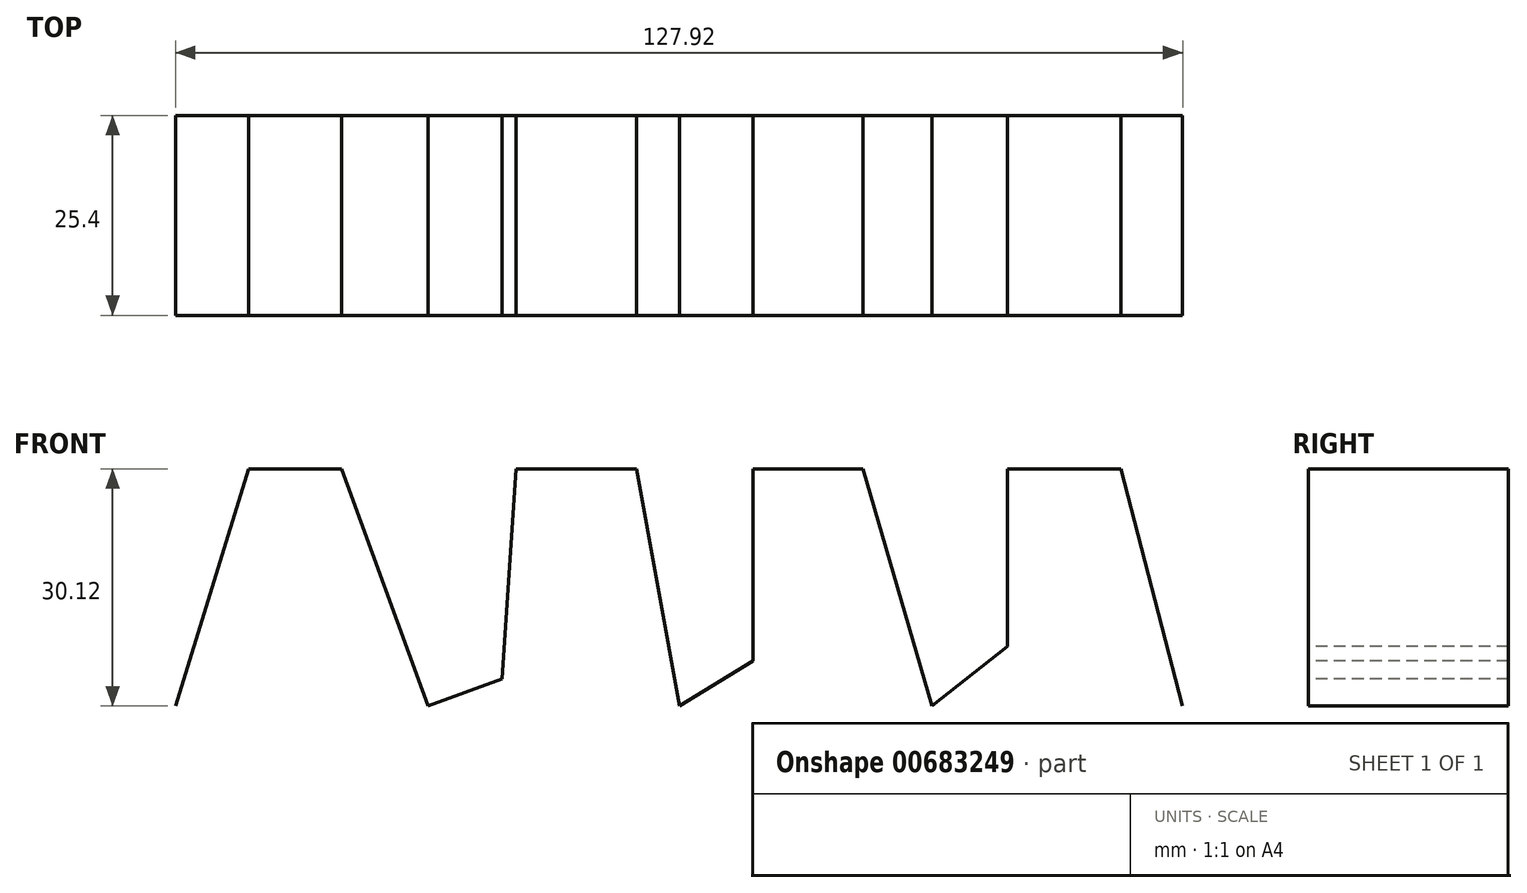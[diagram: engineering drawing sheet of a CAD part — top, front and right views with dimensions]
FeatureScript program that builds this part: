
annotation { "Feature Type Name" : "Feature", "Feature Type Description" : "" }
export const myFeature = defineFeature(function(context is Context, id is Id, definition is map)
    precondition{}
    {
        {
            var Q0;
            Q0=qCreatedBy(makeId("Front.planeOp"),FACE);
            var sketch = newSketch(context, id + "F0", { "sketchPlane" : qUnion([Q0])});
            skLineSegment(sketch, "E0", {"start": v(-63.99, 0) * mm, "end": v(-54.75, 30.12) * mm});
            skLineSegment(sketch, "E1", {"start": v(-54.75, 30.12) * mm, "end": v(-42.93, 30.12) * mm});
            skLineSegment(sketch, "E2", {"start": v(-42.93, 30.12) * mm, "end": v(-31.94, 0) * mm});
            skLineSegment(sketch, "E3", {"start": v(-31.94, 0) * mm, "end": v(-22.51, 3.44) * mm});
            skLineSegment(sketch, "E4", {"start": v(-22.51, 3.44) * mm, "end": v(-20.77, 30.12) * mm});
            skLineSegment(sketch, "E5", {"start": v(-20.77, 30.12) * mm, "end": v(-5.47, 30.12) * mm});
            skLineSegment(sketch, "E6", {"start": v(-5.47, 30.12) * mm, "end": v(0, 0) * mm});
            skLineSegment(sketch, "E7", {"start": v(0, 0) * mm, "end": v(9.35, 5.71) * mm});
            skLineSegment(sketch, "E8", {"start": v(9.35, 5.71) * mm, "end": v(9.35, 30.12) * mm});
            skLineSegment(sketch, "E9", {"start": v(9.35, 30.12) * mm, "end": v(23.32, 30.12) * mm});
            skLineSegment(sketch, "E10", {"start": v(23.32, 30.12) * mm, "end": v(32.05, 0) * mm});
            skLineSegment(sketch, "E11", {"start": v(32.05, 0) * mm, "end": v(41.66, 7.57) * mm});
            skLineSegment(sketch, "E12", {"start": v(41.66, 7.57) * mm, "end": v(41.66, 30.12) * mm});
            skLineSegment(sketch, "E13", {"start": v(41.66, 30.12) * mm, "end": v(56.07, 30.12) * mm});
            skLineSegment(sketch, "E14", {"start": v(56.07, 30.12) * mm, "end": v(63.93, 0) * mm});
            skSolve(sketch);
        }
        {
            var Q0;
            Q0=sQuery(id+"F0.wireOp",EDGE,"E14");
            var Q1;
            Q1=sQuery(id+"F0.wireOp",EDGE,"E13");
            var Q2;
            Q2=sQuery(id+"F0.wireOp",EDGE,"E12");
            var Q3;
            Q3=sQuery(id+"F0.wireOp",EDGE,"E11");
            var Q4;
            Q4=sQuery(id+"F0.wireOp",EDGE,"E10");
            var Q5;
            Q5=sQuery(id+"F0.wireOp",EDGE,"E9");
            var Q6;
            Q6=sQuery(id+"F0.wireOp",EDGE,"E8");
            var Q7;
            Q7=sQuery(id+"F0.wireOp",EDGE,"E7");
            var Q8;
            Q8=sQuery(id+"F0.wireOp",EDGE,"E6");
            var Q9;
            Q9=sQuery(id+"F0.wireOp",EDGE,"E5");
            var Q10;
            Q10=sQuery(id+"F0.wireOp",EDGE,"E4");
            var Q11;
            Q11=sQuery(id+"F0.wireOp",EDGE,"E3");
            var Q12;
            Q12=sQuery(id+"F0.wireOp",EDGE,"E2");
            var Q13;
            Q13=sQuery(id+"F0.wireOp",EDGE,"E1");
            var Q14;
            Q14=sQuery(id+"F0.wireOp",EDGE,"E0");
            extrude(context, id + "F1", {"bodyType" : ToolBodyType.SURFACE, "surfaceEntities" : qUnion([Q0, Q1, Q2, Q3, Q4, Q5, Q6, Q7, Q8, Q9, Q10, Q11, Q12, Q13, Q14]), "depth" : 25.4 * mm, "offsetDistance" : 25.4 * mm});
        }
    });
